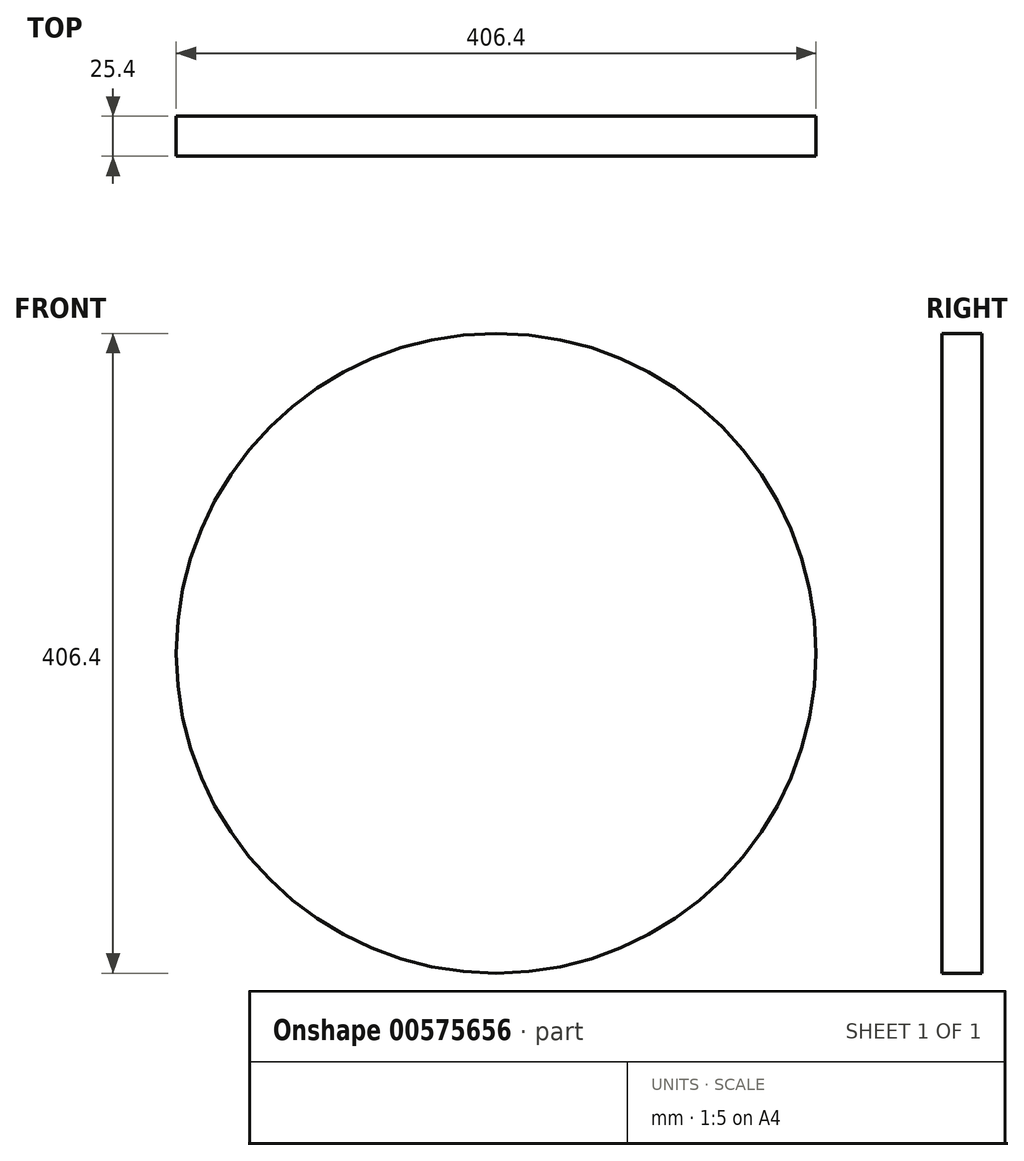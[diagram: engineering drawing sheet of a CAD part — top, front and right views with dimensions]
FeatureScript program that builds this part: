
annotation { "Feature Type Name" : "Feature", "Feature Type Description" : "" }
export const myFeature = defineFeature(function(context is Context, id is Id, definition is map)
    precondition{}
    {
        {
            var Q0;
            Q0=qCreatedBy(makeId("Front.planeOp"),FACE);
            var sketch = newSketch(context, id + "F0", { "sketchPlane" : qUnion([Q0])});
            skLineSegment(sketch, "E0", {"start": v(0, 0) * mm, "end": v(914.4, 0) * mm});
            skLineSegment(sketch, "E1", {"start": v(914.4, 0) * mm, "end": v(914.4, 812.8) * mm});
            skLineSegment(sketch, "E2", {"start": v(914.4, 812.8) * mm, "end": v(0, 812.8) * mm});
            skLineSegment(sketch, "E3", {"start": v(0, 812.8) * mm, "end": v(0, 0) * mm});
            skCircle(sketch, "E4", {"center": v(0, 406.4) * mm, "radius": 203.2 * mm});
            skArc(sketch, "E5", {"start": v(0, 812.8) * mm, "mid": v(-406.4, 406.4) * mm, "end": v(0, 0) * mm});
            skLineSegment(sketch, "E6", {"start": v(914.4, 0) * mm, "end": v(914.4, 203.2) * mm});
            skLineSegment(sketch, "E7", {"start": v(914.4, 203.2) * mm, "end": v(1727.2, 203.2) * mm});
            skLineSegment(sketch, "E8", {"start": v(1727.2, 203.2) * mm, "end": v(1727.2, 609.6) * mm});
            skLineSegment(sketch, "E9", {"start": v(1727.2, 609.6) * mm, "end": v(914.4, 609.6) * mm});
            skSolve(sketch);
        }
        {
            var Q0;
            Q0=sQuery(id+"F0.wireOp",EDGE,"E4");
            extrude(context, id + "F1", {"bodyType" : ToolBodyType.SURFACE, "surfaceEntities" : qUnion([Q0]), "depth" : 25.4 * mm, "offsetDistance" : 25.4 * mm});
        }
    });
